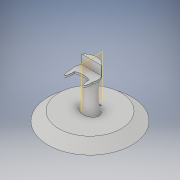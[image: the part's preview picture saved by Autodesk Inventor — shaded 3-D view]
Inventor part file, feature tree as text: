
AUTODESK INVENTOR PART (.ipt)
format: ipt  version: 2017 (Build 210142000, 142)  size: 549,888 bytes
history: native  units: in
note: dims shown in document units (in); Inventor stores cm internally (conversion verified against a paired STEP export)
features: other x13, sketch x9, extrude x6, loft x2, fillet x1, plane x1
ambient origin geometry x7: Origin, YZ Plane, XY Plane, X Axis, Y Axis, Z Axis, Center Point
bodies: Body1 (feature_tree)
feature tree (32):
  other  "bace + terminal"
  other  "bace of terminal"
  other  "middle workplane"
  other  "middle"
  other  "top workplane"
  loft  "curved tower"
  extrude  "arm rests and terminal monitor"  Depth=0.8in
  other  "middle of the part vertical"
  other  "used to line up the key board and mouse"
  extrude  "bace"  Depth=1.8247in
  other  "ramp around"
  other  "mate to back to monitor"
  extrude  "monitor raise"  Depth=1.0in
  fillet  "curve edges"  Radius=1.2in
  sketch  "Sketch26"  dims[d8=0.0in d9=90.0deg d10=0.0in d11=90.0deg d12=0.0in d13=90.0deg d19=1.2in]
  plane  "Work Plane16"
  loft  "outlet cap"
  sketch  "Sketch28"  dims[d28=0.75in d29=1.0in]
  extrude  "outlet revele out"  Depth=1.0in
  extrude  "hot and ground wire holes"  Depth=0.0108in
  other  "screw workplane"
  other  "screw made"
  extrude  "slot for screw"  Depth=1.0in TaperAngle=0.0deg
  other  "bottom workplane"
  other  "top"
  sketch  "Sketch15"  dims[d0=1.0in d1=0.75in]
  sketch  "Sketch17"  dims[d2=1.8247in d3=0.8in]
  sketch  "Sketch23"  dims[d4=0.55in d5=1.8247in]
  sketch  "Sketch25"  dims[d6=0.75in d7=1.0in]
  sketch  "Sketch27"  dims[d20=0.85in d27=1.1in]
  sketch  "Sketch29"  dims[d30=0.65in]
  sketch  "Sketch30"  dims[d42=1.1in d43=0.85in d44=1.0in d45=0.75in d49=1.2in d50=0.85in d51=1.0in d52=0.75in d122=7.0in d123=1.0in d124=0.0in d141=0.2749in d142=90.0deg d163=0.8125in d165=0.4167in d166=0.8125in d167=0.4167in d168=0.2083in d169=0.0in d170=1.125in d173=1.8892in d174=1.1844in d175=1.125in d176=1.125in d177=1.1844in d178=1.0in d179=0.0in d180=0.5527in d181=0.01in d182=0.2318in d183=0.3777in d184=0.0181in d185=0.05in d186=0.0678in d188=0.1962in d189=0.3421in d190=0.0in d191=90.0deg d192=0.0in d193=90.0deg d194=0.0251in d195=0.0305in d197=0.0931in d198=0.0311in d199=0.0362in d200=0.0045in d201=0.0208in d202=0.0208in d203=0.0078in d204=0.0291in d205=0.0078in d206=0.0362in d207=0.0045in d208=0.0208in d209=0.0078in d211=0.0078in d212=0.0208in d213=0.0181in d214=0.0291in d221=0.003in d222=0.0in d223=0.0649in d224=0.0in d225=90.0deg d226=0.0108in d227=0.0027in d228=90.0deg d229=0.0015in d230=0.0128in d231=0.0in]
